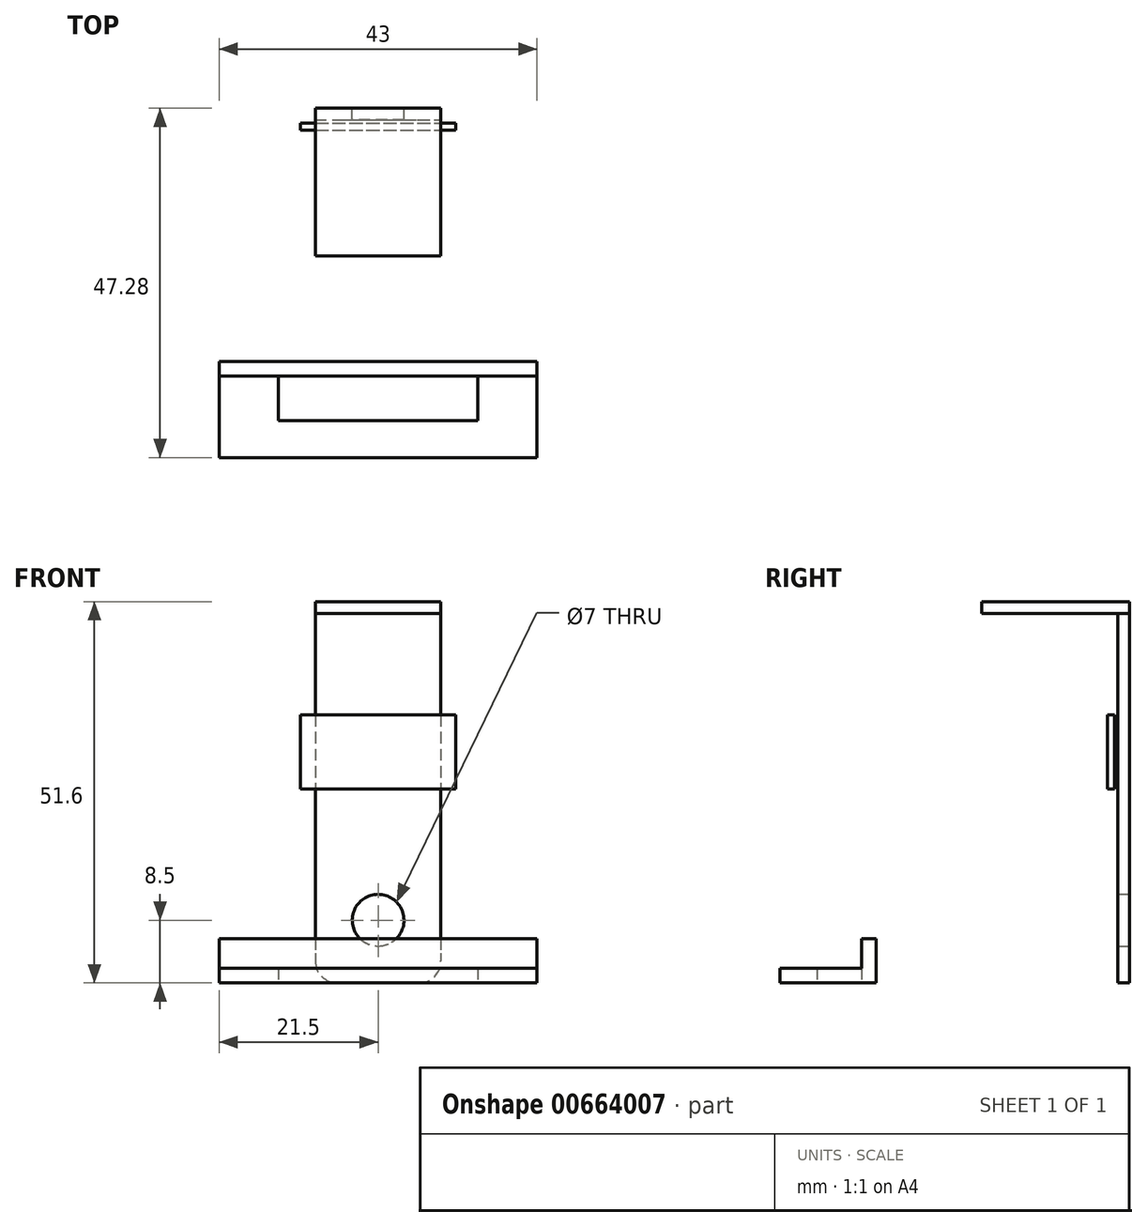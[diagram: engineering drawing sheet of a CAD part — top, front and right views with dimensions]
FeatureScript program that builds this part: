
annotation { "Feature Type Name" : "Feature", "Feature Type Description" : "" }
export const myFeature = defineFeature(function(context is Context, id is Id, definition is map)
    precondition{}
    {
        {
            var Q0;
            Q0=qCreatedBy(makeId("Front.planeOp"),FACE);
            cPlane(context, id + "F0", {"entities" : qUnion([Q0]), "cplaneType" : CPlaneType.OFFSET, "offset" : 2 * mm, "width" : 150 * mm, "height" : 150 * mm});
        }
        {
            var Q0;
            Q0=qCreatedBy(id+"F0.planeOp",FACE);
            var sketch = newSketch(context, id + "F1", { "sketchPlane" : qUnion([Q0])});
            skLineSegment(sketch, "E0.bottom", {"start": v(-2, 36.28) * mm, "end": v(19, 36.28) * mm});
            skLineSegment(sketch, "E0.top", {"start": v(-2, 26.28) * mm, "end": v(19, 26.28) * mm});
            skLineSegment(sketch, "E0.left", {"start": v(-2, 36.28) * mm, "end": v(-2, 26.28) * mm});
            skLineSegment(sketch, "E0.right", {"start": v(19, 36.28) * mm, "end": v(19, 26.28) * mm});
            skPoint(sketch, "E1", {"position": v(8.5, 36.28) * mm});
            skSolve(sketch);
        }
        {
            var Q0;
            Q0=qCreatedBy(makeId("Front.planeOp"),FACE);
            var sketch = newSketch(context, id + "F2", { "sketchPlane" : qUnion([Q0])});
            skLineSegment(sketch, "E2.bottom", {"start": v(0, 50) * mm, "end": v(17, 50) * mm});
            skLineSegment(sketch, "E2.top", {"start": v(3, 0) * mm, "end": v(14, 0) * mm});
            skLineSegment(sketch, "E2.left", {"start": v(0, 50) * mm, "end": v(0, 3) * mm});
            skLineSegment(sketch, "E2.right", {"start": v(17, 50) * mm, "end": v(17, 3) * mm});
            skCircle(sketch, "E3", {"center": v(8.5, 8.5) * mm, "radius": 3.5 * mm});
            skPoint(sketch, "E4.visualSharp", {"position": v(0, 0) * mm});
            skArc(sketch, "E4.filletArc", {"start": v(0, 3) * mm, "mid": v(0.88, 0.88) * mm, "end": v(3, 0) * mm});
            skPoint(sketch, "E5.visualSharp", {"position": v(17, 0) * mm});
            skArc(sketch, "E5.filletArc", {"start": v(14, 0) * mm, "mid": v(16.12, 0.88) * mm, "end": v(17, 3) * mm});
            skPoint(sketch, "E6", {"position": v(8.5, 0) * mm});
            skLineSegment(sketch, "E7", {"start": v(0, 17) * mm, "end": v(17, 17) * mm});
            skLineSegment(sketch, "E8", {"start": v(0, 22) * mm, "end": v(17, 22) * mm});
            skSolve(sketch);
        }
        {
            var Q0;
            Q0=sQuery(id+"F2.wireOp",EDGE,"E2.bottom");
            cPlane(context, id + "F3", {"entities" : qUnion([Q0]), "cplaneType" : CPlaneType.LINE_ANGLE, "offset" : 25 * mm, "angle" : 90 * degree, "width" : 150 * mm, "height" : 150 * mm});
        }
        {
            var Q0;
            Q0=qCreatedBy(id+"F3.planeOp",FACE);
            var sketch = newSketch(context, id + "F4", { "sketchPlane" : qUnion([Q0])});
            skLineSegment(sketch, "E9.bottom", {"start": v(0, 0) * mm, "end": v(17, 0) * mm});
            skLineSegment(sketch, "E9.top", {"start": v(0, -20) * mm, "end": v(17, -20) * mm});
            skLineSegment(sketch, "E9.left", {"start": v(0, 0) * mm, "end": v(0, -20) * mm});
            skLineSegment(sketch, "E9.right", {"start": v(17, 0) * mm, "end": v(17, -20) * mm});
            skSolve(sketch);
        }
        {
            var Q0;
            Q0=qCreatedBy(makeId("Top.planeOp"),FACE);
            var sketch = newSketch(context, id + "F5", { "sketchPlane" : qUnion([Q0])});
            skLineSegment(sketch, "E10.bottom", {"start": v(-13, -36.28) * mm, "end": v(30, -36.28) * mm});
            skLineSegment(sketch, "E10.top", {"start": v(-13, -47.28) * mm, "end": v(30, -47.28) * mm});
            skLineSegment(sketch, "E10.left", {"start": v(-13, -36.28) * mm, "end": v(-13, -47.28) * mm});
            skLineSegment(sketch, "E10.right", {"start": v(30, -36.28) * mm, "end": v(30, -47.28) * mm});
            skPoint(sketch, "E11", {"position": v(8.5, -36.28) * mm});
            skLineSegment(sketch, "E12.bottom", {"start": v(-5, -36.28) * mm, "end": v(22, -36.28) * mm});
            skLineSegment(sketch, "E12.top", {"start": v(-5, -42.28) * mm, "end": v(22, -42.28) * mm});
            skLineSegment(sketch, "E12.left", {"start": v(-5, -36.28) * mm, "end": v(-5, -42.28) * mm});
            skLineSegment(sketch, "E12.right", {"start": v(22, -36.28) * mm, "end": v(22, -42.28) * mm});
            skSolve(sketch);
        }
        {
            var Q0;
            Q0=sQuery(id+"F5.wireOp",EDGE,"E10.bottom");
            cPlane(context, id + "F6", {"entities" : qUnion([Q0]), "cplaneType" : CPlaneType.LINE_ANGLE, "offset" : 25 * mm, "angle" : 0 * degree, "width" : 150 * mm, "height" : 150 * mm});
        }
        {
            var Q0;
            Q0=qCreatedBy(id+"F6.planeOp",FACE);
            var sketch = newSketch(context, id + "F7", { "sketchPlane" : qUnion([Q0])});
            skLineSegment(sketch, "E13.bottom", {"start": v(13, 6) * mm, "end": v(-30, 6) * mm});
            skLineSegment(sketch, "E13.top", {"start": v(13, 0) * mm, "end": v(-30, 0) * mm});
            skLineSegment(sketch, "E13.left", {"start": v(13, 6) * mm, "end": v(13, 0) * mm});
            skLineSegment(sketch, "E13.right", {"start": v(-30, 6) * mm, "end": v(-30, 0) * mm});
            skSolve(sketch);
        }
        {
            var Q0;
            Q0=makeQuery(id+"F5.imprint","IMPRINT",FACE,{"disambiguationData":[TD([[makeQuery(id+"F5.imprint","IMPRINT",EDGE,{"derivedFrom":sQuery(id+"F5.wireOp",EDGE,"E10.top")}),1.0]])]});
            extrude(context, id + "F8", {"entities" : qUnion([Q0]), "depth" : 2 * mm, "offsetDistance" : 25 * mm});
        }
        {
            var Q0;
            Q0=makeQuery(id+"F7.imprint","IMPRINT",FACE,{"disambiguationData":[TD([[makeQuery(id+"F7.imprint","IMPRINT",EDGE,{"derivedFrom":sQuery(id+"F7.wireOp",EDGE,"E13.bottom")}),1.0]])]});
            extrude(context, id + "F9", {"entities" : qUnion([Q0]), "operationType" : NewBodyOperationType.ADD, "depth" : 2 * mm, "offsetDistance" : 25 * mm});
        }
        {
            var Q0;
            Q0=makeQuery(id+"F2.imprint","IMPRINT",FACE,{"disambiguationData":[TD([[makeQuery(id+"F2.imprint","IMPRINT",EDGE,{"derivedFrom":sQuery(id+"F2.wireOp",EDGE,"E2.top")}),1.0]])]});
            var Q1;
            {var subQ0=sQuery(id+"F2.wireOp",EDGE,"E7");Q1=makeQuery(id+"F2.imprint","IMPRINT",FACE,{"disambiguationData":[TD([[makeQuery(id+"F2.imprint","IMPRINT",EDGE,{"derivedFrom":subQ0}),1.0]])]});}
            var Q2;
            {var subQ6=sQuery(id+"F2.wireOp",EDGE,"Dp6an8a6-R08j-VOmp-96o3-zJHUd0OIUKr1.top");Q2=makeQuery(id+"F2.imprint","IMPRINT",FACE,{"disambiguationData":[TD([[makeQuery(id+"F2.imprint","IMPRINT",EDGE,{"derivedFrom":subQ6}),-1.0]])]});}
            var Q3;
            {var subQ1=sQuery(id+"F2.wireOp",EDGE,"E2.bottom");Q3=makeQuery(id+"F2.imprint","IMPRINT",FACE,{"disambiguationData":[TD([[makeQuery(id+"F2.imprint","IMPRINT",EDGE,{"derivedFrom":subQ1}),-1.0]])]});}
            extrude(context, id + "F10", {"entities" : qUnion([Q0, Q1, Q2, Q3]), "depth" : 1.6 * mm, "offsetDistance" : 25 * mm});
        }
        {
            var Q0;
            Q0=makeQuery(id+"F4.imprint","IMPRINT",FACE,{"disambiguationData":[TD([[makeQuery(id+"F4.imprint","IMPRINT",EDGE,{"derivedFrom":sQuery(id+"F4.wireOp",EDGE,"E9.bottom")}),-1.0]])]});
            extrude(context, id + "F11", {"entities" : qUnion([Q0]), "depth" : 1.6 * mm, "offsetDistance" : 25 * mm});
        }
        {
            var Q0;
            Q0=makeQuery(id+"F1.imprint","IMPRINT",FACE,{"disambiguationData":[TD([[makeQuery(id+"F1.imprint","IMPRINT",EDGE,{"derivedFrom":sQuery(id+"F1.wireOp",EDGE,"E0.bottom")}),-1.0]])]});
            extrude(context, id + "F12", {"entities" : qUnion([Q0]), "depth" : 1 * mm, "offsetDistance" : 25 * mm});
        }
    });
